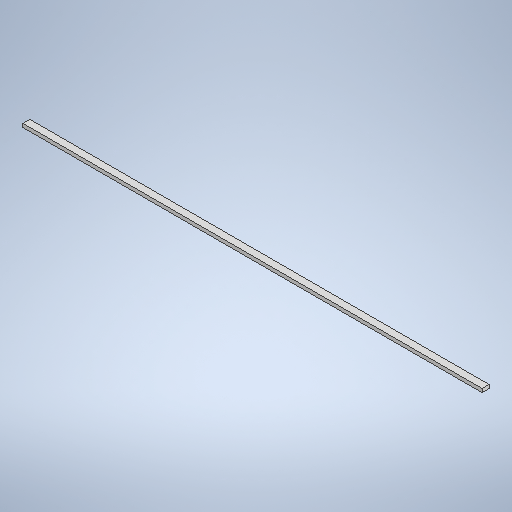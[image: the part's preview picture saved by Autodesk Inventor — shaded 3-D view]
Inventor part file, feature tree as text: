
AUTODESK INVENTOR PART (.ipt)
format: ipt  version: 2025.2 (Build 292293000, 293)  size: 232,448 bytes
history: native  units: mm
features: extrude x1, sketch x1
ambient origin geometry x8: Origin, YZ Plane, XZ Plane, XY Plane, X Axis, Y Axis, Z Axis, Center Point
bodies: Solid1 (feature_tree)
feature tree (2):
  extrude  "Extrusion1"  Depth=10.0mm TaperAngle=0.0deg
  sketch  "Sketch1"  dims[d0=660.0mm d1=10.0mm d2=0.0mm]
